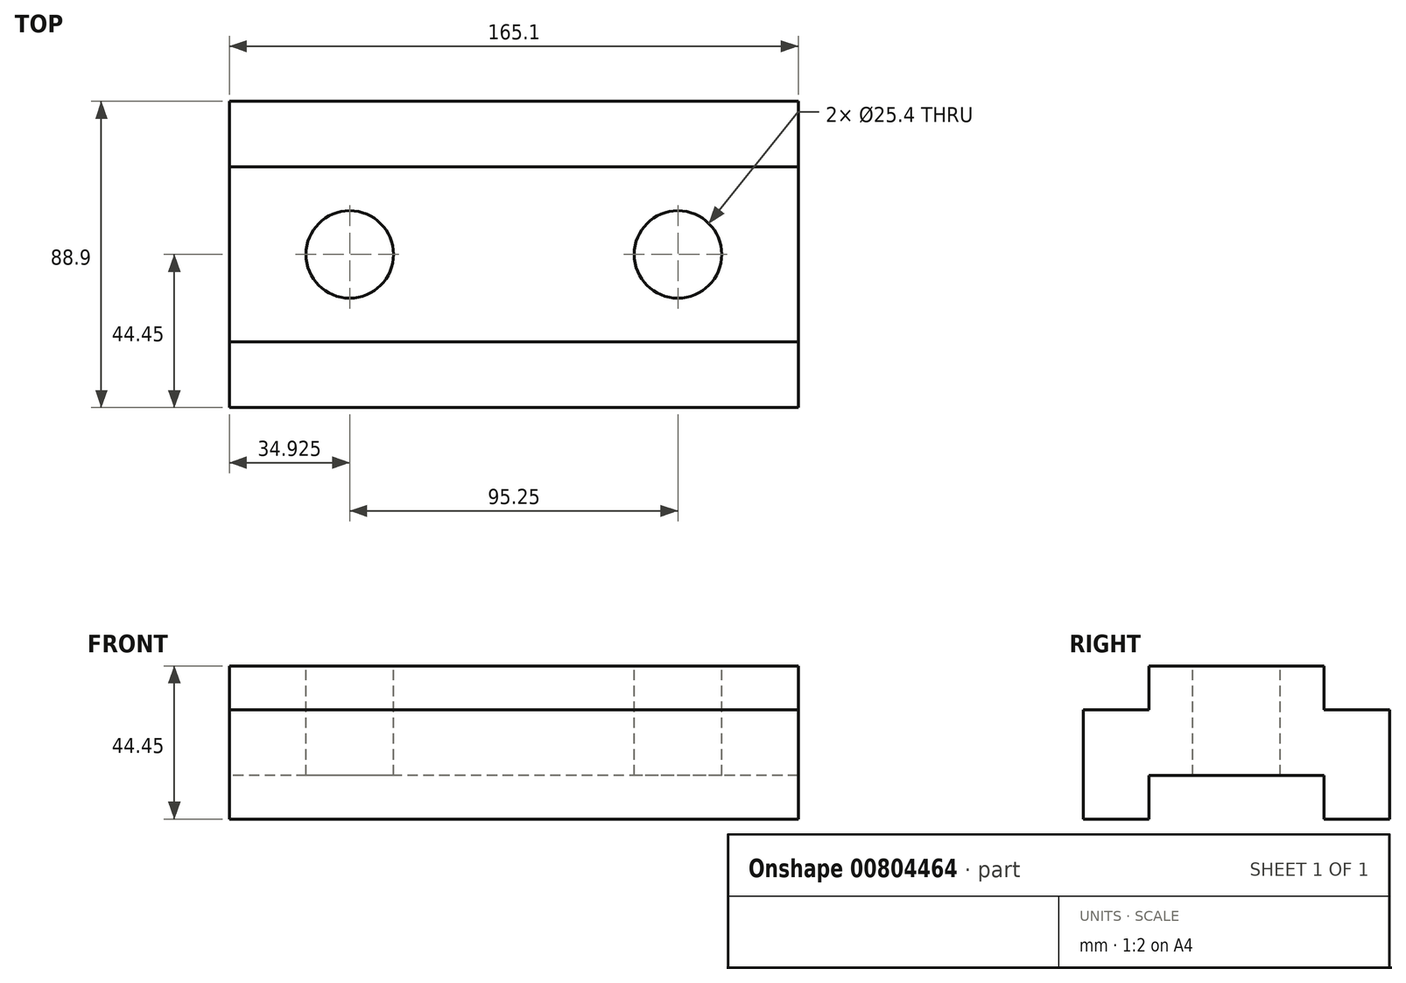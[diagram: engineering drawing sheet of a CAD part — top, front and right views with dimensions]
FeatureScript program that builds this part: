
annotation { "Feature Type Name" : "Feature", "Feature Type Description" : "" }
export const myFeature = defineFeature(function(context is Context, id is Id, definition is map)
    precondition{}
    {
        {
            var Q0;
            Q0=qCreatedBy(makeId("Right.planeOp"),FACE);
            var sketch = newSketch(context, id + "F0", { "sketchPlane" : qUnion([Q0])});
            skLineSegment(sketch, "E0", {"start": v(0, 0) * mm, "end": v(19.05, 0) * mm});
            skLineSegment(sketch, "E1", {"start": v(19.05, 0) * mm, "end": v(19.05, 12.7) * mm});
            skLineSegment(sketch, "E2", {"start": v(19.05, 12.7) * mm, "end": v(69.85, 12.7) * mm});
            skLineSegment(sketch, "E3", {"start": v(69.85, 12.7) * mm, "end": v(69.85, 0) * mm});
            skLineSegment(sketch, "E4", {"start": v(69.85, 0) * mm, "end": v(88.9, 0) * mm});
            skLineSegment(sketch, "E5", {"start": v(0, 0) * mm, "end": v(0, 31.75) * mm});
            skLineSegment(sketch, "E6", {"start": v(0, 31.75) * mm, "end": v(19.05, 31.75) * mm});
            skLineSegment(sketch, "E7", {"start": v(19.05, 31.75) * mm, "end": v(19.05, 44.45) * mm});
            skLineSegment(sketch, "E8", {"start": v(19.05, 44.45) * mm, "end": v(69.85, 44.45) * mm});
            skLineSegment(sketch, "E9", {"start": v(69.85, 44.45) * mm, "end": v(69.85, 31.75) * mm});
            skLineSegment(sketch, "E10", {"start": v(69.85, 31.75) * mm, "end": v(88.9, 31.75) * mm});
            skLineSegment(sketch, "E11", {"start": v(88.9, 31.75) * mm, "end": v(88.9, 0) * mm});
            skSolve(sketch);
        }
        {
            var Q0;
            Q0 = qSketchRegion(id + "F0", true);
            extrude(context, id + "F1", {"entities" : qUnion([Q0]), "depth" : 165.1 * mm, "offsetDistance" : 25.4 * mm});
        }
        {
            var Q0;
            Q0=makeQuery(id+"F1.opExtrude","SWEPT_FACE",FACE,{"disambiguationData":[OSD([sQuery(id+"F0.wireOp",EDGE,"E8")])]});
            var sketch = newSketch(context, id + "F2", { "sketchPlane" : qUnion([Q0])});
            skLineSegment(sketch, "E12", {"start": v(0, 69.85) * mm, "end": v(0, 44.45) * mm, "construction": true});
            skLineSegment(sketch, "E13", {"start": v(0, 44.45) * mm, "end": v(34.93, 44.45) * mm, "construction": true});
            skLineSegment(sketch, "E14", {"start": v(34.93, 44.45) * mm, "end": v(130.18, 44.45) * mm, "construction": true});
            skCircle(sketch, "E15", {"center": v(34.93, 44.45) * mm, "radius": 12.7 * mm});
            skCircle(sketch, "E16", {"center": v(130.18, 44.45) * mm, "radius": 12.7 * mm});
            skSolve(sketch);
        }
        {
            var Q0;
            Q0 = qSketchRegion(id + "F2", true);
            extrude(context, id + "F3", {"entities" : qUnion([Q0]), "operationType" : NewBodyOperationType.REMOVE, "endBound" : BoundingType.UP_TO_NEXT, "oppositeDirection" : true, "depth" : 25.4 * mm, "offsetDistance" : 25.4 * mm});
        }
    });
